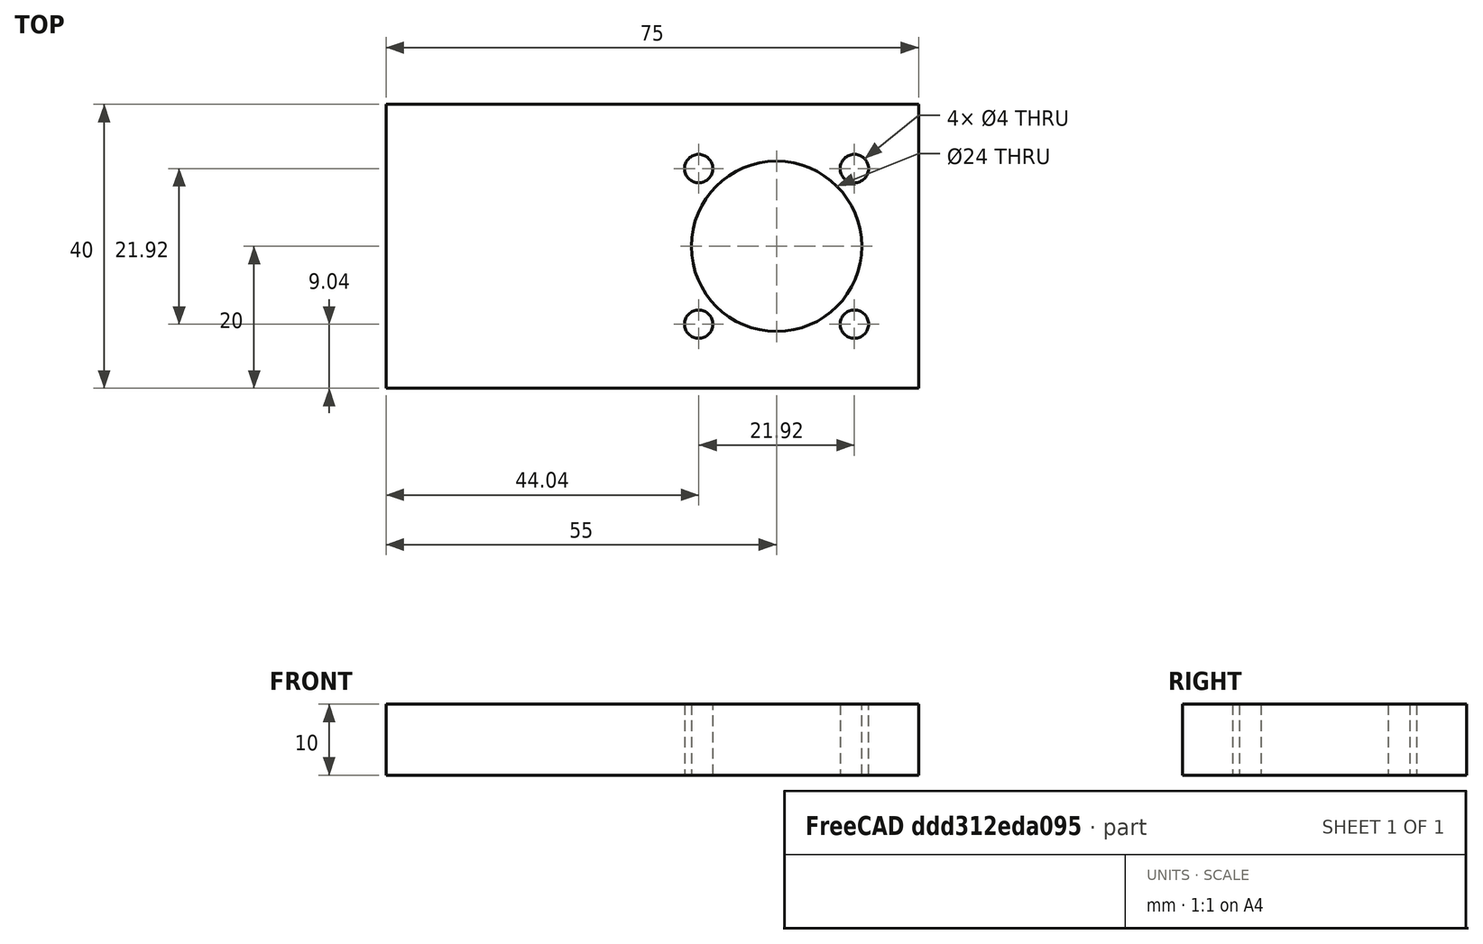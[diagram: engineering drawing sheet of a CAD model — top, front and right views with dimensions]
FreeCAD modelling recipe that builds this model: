
FCSTD DOCUMENT  (FreeCAD 0.21R33771 (Git))
Label: StaffaChiocciola16x4
License: All rights reserved
LicenseURL: http://en.wikipedia.org/wiki/All_rights_reserved
objects: Sketcher::SketchObject×1, PartDesign::Pad×1, PartDesign::CoordinateSystem×1, PartDesign::Body×1
note: 5 computed .brp shape members not serialized (recipe doc carries the construction recipe); baked Part::Feature solids carry a one-line shape summary decoded from their .brp

FEATURE [Sketcher::SketchObject] Sketch
  FullyConstrained = false
  MapMode = 5
  Support = -> [XY_Plane]
  sketch-geometry (12):
    g0: LineSegment StartX=0 StartY=0 StartZ=0 EndX=75 EndY=0 EndZ=0
    g1: LineSegment StartX=75 StartY=0 StartZ=0 EndX=75 EndY=40 EndZ=0
    g2: LineSegment StartX=75 StartY=40 StartZ=0 EndX=0 EndY=40 EndZ=0
    g3: LineSegment StartX=0 StartY=40 StartZ=0 EndX=0 EndY=0 EndZ=0
    g4: Circle CenterX=55 CenterY=20 CenterZ=0 NormalX=0 NormalY=0 NormalZ=1 AngleXU=0 Radius=12
    g5: Circle CenterX=55 CenterY=20 CenterZ=0 NormalX=0 NormalY=0 NormalZ=1 AngleXU=0 Radius=15.5
    g6: Circle CenterX=65.9602 CenterY=30.9602 CenterZ=0 NormalX=0 NormalY=0 NormalZ=1 AngleXU=0 Radius=2
    g7: Circle CenterX=44.0398 CenterY=30.9602 CenterZ=0 NormalX=0 NormalY=0 NormalZ=1 AngleXU=0 Radius=2
    g8: Circle CenterX=44.0398 CenterY=9.03984 CenterZ=0 NormalX=0 NormalY=0 NormalZ=1 AngleXU=0 Radius=2
    g9: Circle CenterX=65.9602 CenterY=9.03984 CenterZ=0 NormalX=0 NormalY=0 NormalZ=1 AngleXU=0 Radius=2
    g10: LineSegment StartX=84.4263 StartY=-9.42631 StartZ=0 EndX=2.27454 EndY=72.7255 EndZ=0
    g11: LineSegment StartX=67.5573 StartY=32.5573 StartZ=0 EndX=12.7075 EndY=-22.2925 EndZ=0
  constraints (32):
    c: Coincident(g0,g1)
    c: Coincident(g2,g3)
    c: Coincident(g3,g0)
    c: Horizontal(g0)
    c: Horizontal(g2)
    c: Vertical(g1)
    c: Vertical(g3)
    c: Coincident(g0,g-1)
    c: DistanceY(g3,g3) = 40
    c: Radius(g4) = 12
    c: DistanceX(g4,g0) = 20
    c: DistanceY(g0,g4) = 20
    c: Coincident(g5,g4)
    c: PointOnObject(g6,g5)
    c: PointOnObject(g7,g5)
    c: PointOnObject(g8,g5)
    c: PointOnObject(g9,g5)
    c: Equal(g6,g7)
    c: Equal(g7,g8)
    c: Equal(g8,g9)
    c: Radius(g6) = 2
    c: Tangent(g7,g10) = 1.5708
    c: PointOnObject(g4,g10)
    c: PointOnObject(g9,g10)
    c: PointOnObject(g4,g11)
    c: PointOnObject(g6,g11)
    c: PointOnObject(g8,g11)
    c: Radius(g5) = 15.5
    c: Angle(g10,g11) = 1.5708
    c: Angle(g11,g0) = 2.35619
    c: Coincident(g2,g1)
    c: DistanceX(g0,g0) = 75
FEATURE [PartDesign::Pad] Pad
  Direction = (0,0,1)
  Length = 10
  Length2 = 10
  Profile = -> Sketch
  ReferenceAxis = -> Sketch [N_Axis]
  Type = 0
FEATURE [PartDesign::CoordinateSystem] LCS_StaffaChiocciola16x4
  AttacherType = Attacher::AttachEngine3D
FEATURE [PartDesign::Body] Body  label="Corpo"
  Group = -> [Sketch,Pad,LCS_StaffaChiocciola16x4]
  Origin = -> Origin
  Tip = -> Pad
